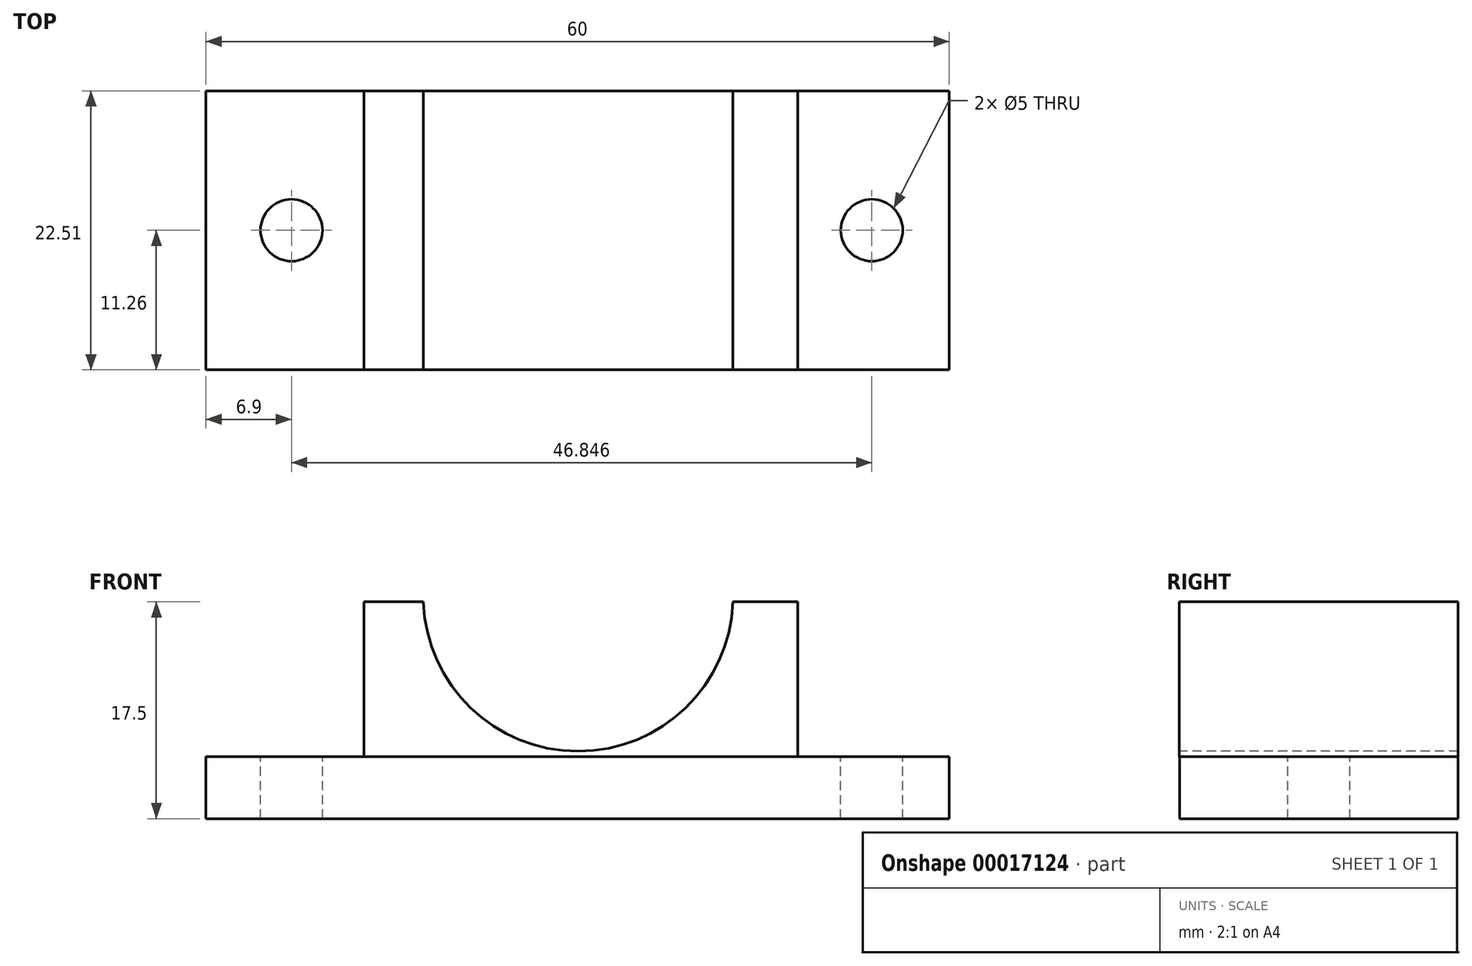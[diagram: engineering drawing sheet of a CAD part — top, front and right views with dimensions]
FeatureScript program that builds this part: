
annotation { "Feature Type Name" : "Feature", "Feature Type Description" : "" }
export const myFeature = defineFeature(function(context is Context, id is Id, definition is map)
    precondition{}
    {
        {
            var Q0;
            Q0=qCreatedBy(makeId("Front.planeOp"),FACE);
            var sketch = newSketch(context, id + "F0", { "sketchPlane" : qUnion([Q0])});
            skLineSegment(sketch, "E0.bottom", {"start": v(-24.82, 19.98) * mm, "end": v(35.18, 19.98) * mm});
            skLineSegment(sketch, "E0.top", {"start": v(-24.82, 14.98) * mm, "end": v(35.18, 14.98) * mm});
            skLineSegment(sketch, "E0.left", {"start": v(-24.82, 19.98) * mm, "end": v(-24.82, 14.98) * mm});
            skLineSegment(sketch, "E0.right", {"start": v(35.18, 19.98) * mm, "end": v(35.18, 14.98) * mm});
            skSolve(sketch);
        }
        {
            var Q0;
            Q0 = qSketchRegion(id + "F0", true);
            extrude(context, id + "F1", {"entities" : qUnion([Q0]), "depth" : 22.5 * mm});
        }
        {
            var Q0;
            Q0=makeQuery(id+"F1.opExtrude","SWEPT_FACE",FACE,{"disambiguationData":[OSD([sQuery(id+"F0.wireOp",EDGE,"E0.bottom")])]});
            var sketch = newSketch(context, id + "F2", { "sketchPlane" : qUnion([Q0])});
            skCircle(sketch, "E1", {"center": v(-17.92, -11.25) * mm, "radius": 2.5 * mm});
            skCircle(sketch, "E2", {"center": v(28.93, -11.25) * mm, "radius": 2.5 * mm});
            skSolve(sketch);
        }
        {
            var Q0;
            Q0 = qSketchRegion(id + "F2", true);
            var Q1;
            Q1 = qConstructionFilter(qBodyType(qCreatedBy(id + "F2" ,EDGE), BodyType.WIRE), ConstructionObject.NO);
            extrude(context, id + "F3", {"entities" : qUnion([Q0]), "operationType" : NewBodyOperationType.REMOVE, "surfaceEntities" : qUnion([Q1]), "oppositeDirection" : true, "depth" : 25.47 * mm});
        }
        {
            var Q0;
            Q0=makeQuery(id+"F2.imprint","IMPRINT",FACE,{"disambiguationData":[TD([[makeQuery(id+"F2.imprint","IMPRINT",EDGE,{"derivedFrom":sQuery(id+"F2.wireOp",EDGE,"E1")}),-1.0]])]});
            var sketch = newSketch(context, id + "F4", { "sketchPlane" : qUnion([Q0])});
            skLineSegment(sketch, "E3.bottom", {"start": v(-12.06, 0) * mm, "end": v(22.94, 0) * mm});
            skLineSegment(sketch, "E3.top", {"start": v(-12.06, -22.51) * mm, "end": v(22.94, -22.51) * mm});
            skLineSegment(sketch, "E3.left", {"start": v(-12.06, 0) * mm, "end": v(-12.06, -22.51) * mm});
            skLineSegment(sketch, "E3.right", {"start": v(22.94, 0) * mm, "end": v(22.94, -22.51) * mm});
            skSolve(sketch);
        }
        {
            var Q0;
            Q0 = qSketchRegion(id + "F4", true);
            extrude(context, id + "F5", {"entities" : qUnion([Q0]), "operationType" : NewBodyOperationType.ADD, "depth" : 12.5 * mm});
        }
        {
            var Q0;
            Q0=makeQuery(id+"F5.opExtrude","SWEPT_FACE",FACE,{"disambiguationData":[OSD([sQuery(id+"F4.wireOp",EDGE,"E3.top")])]});
            var sketch = newSketch(context, id + "F6", { "sketchPlane" : qUnion([Q0])});
            skArc(sketch, "E4", {"start": v(-7.27, 32.48) * mm, "mid": v(5.22, 20.42) * mm, "end": v(17.71, 32.48) * mm});
            skSolve(sketch);
        }
        {
            var Q0;
            {var subQ1=sQuery(id+"F6.wireOp",EDGE,"E4");Q0=makeQuery(id+"F6.imprint","IMPRINT",FACE,{"disambiguationData":[TD([[makeQuery(id+"F6.imprint","IMPRINT",EDGE,{"derivedFrom":subQ1}),1.0]])]});}
            extrude(context, id + "F7", {"entities" : qUnion([Q0]), "operationType" : NewBodyOperationType.REMOVE, "oppositeDirection" : true, "depth" : 30.07 * mm});
        }
    });
